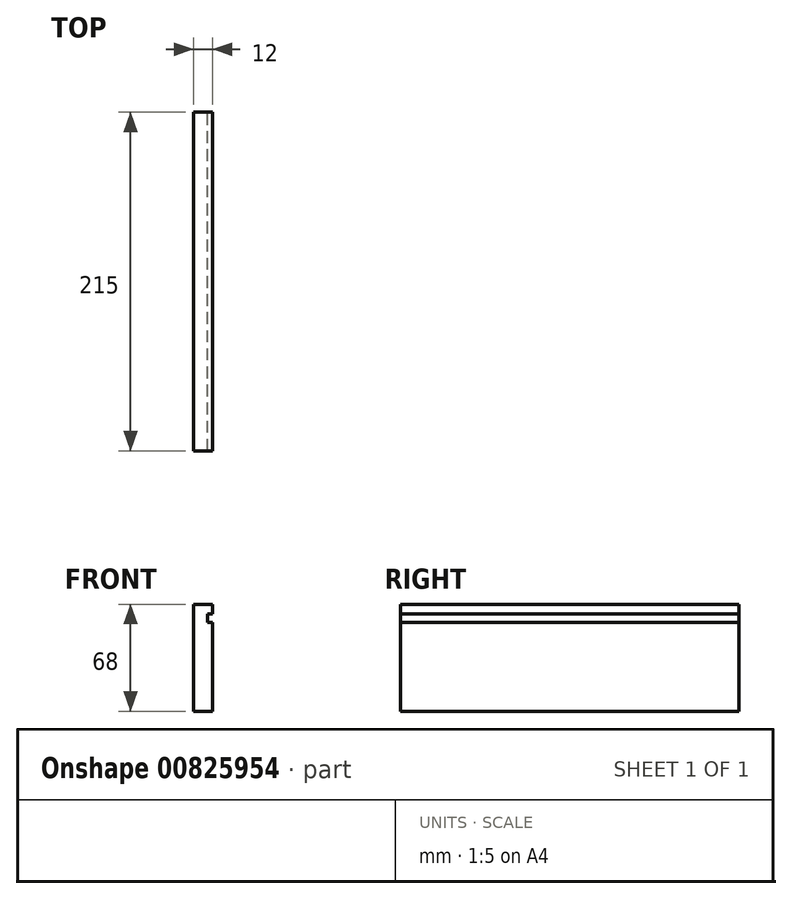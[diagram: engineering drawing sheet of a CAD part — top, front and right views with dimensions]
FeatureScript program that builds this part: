
annotation { "Feature Type Name" : "Feature", "Feature Type Description" : "" }
export const myFeature = defineFeature(function(context is Context, id is Id, definition is map)
    precondition{}
    {
        {
            var Q0;
            Q0=qCreatedBy(makeId("Right.planeOp"),FACE);
            var sketch = newSketch(context, id + "F0", { "sketchPlane" : qUnion([Q0])});
            skLineSegment(sketch, "E0.bottom", {"start": v(-107.5, 34) * mm, "end": v(107.5, 34) * mm});
            skLineSegment(sketch, "E0.top", {"start": v(-107.5, -34) * mm, "end": v(107.5, -34) * mm});
            skLineSegment(sketch, "E0.left", {"start": v(-107.5, 34) * mm, "end": v(-107.5, -34) * mm});
            skLineSegment(sketch, "E0.right", {"start": v(107.5, 34) * mm, "end": v(107.5, -34) * mm});
            skPoint(sketch, "E0.middle", {"position": v(0, 0) * mm});
            skSolve(sketch);
        }
        {
            var Q0;
            Q0 = qSketchRegion(id + "F0", true);
            extrude(context, id + "F1", {"entities" : qUnion([Q0]), "depth" : 12 * mm, "offsetDistance" : 25.4 * mm});
        }
        {
            var Q0;
            Q0=makeQuery(id+"F1.opExtrude","SWEPT_FACE",FACE,{"disambiguationData":[OSD([sQuery(id+"F0.wireOp",EDGE,"E0.right")])]});
            var sketch = newSketch(context, id + "F2", { "sketchPlane" : qUnion([Q0])});
            skLineSegment(sketch, "E1.bottom", {"start": v(-12, 27.98) * mm, "end": v(-9, 27.98) * mm});
            skLineSegment(sketch, "E1.top", {"start": v(-12, 22.36) * mm, "end": v(-9, 22.36) * mm});
            skLineSegment(sketch, "E1.left", {"start": v(-12, 27.98) * mm, "end": v(-12, 22.36) * mm});
            skLineSegment(sketch, "E1.right", {"start": v(-9, 27.98) * mm, "end": v(-9, 22.36) * mm});
            skSolve(sketch);
        }
        {
            var Q0;
            Q0 = qSketchRegion(id + "F2", true);
            extrude(context, id + "F3", {"entities" : qUnion([Q0]), "operationType" : NewBodyOperationType.REMOVE, "oppositeDirection" : true, "depth" : 300 * mm, "offsetDistance" : 25.4 * mm});
        }
    });
